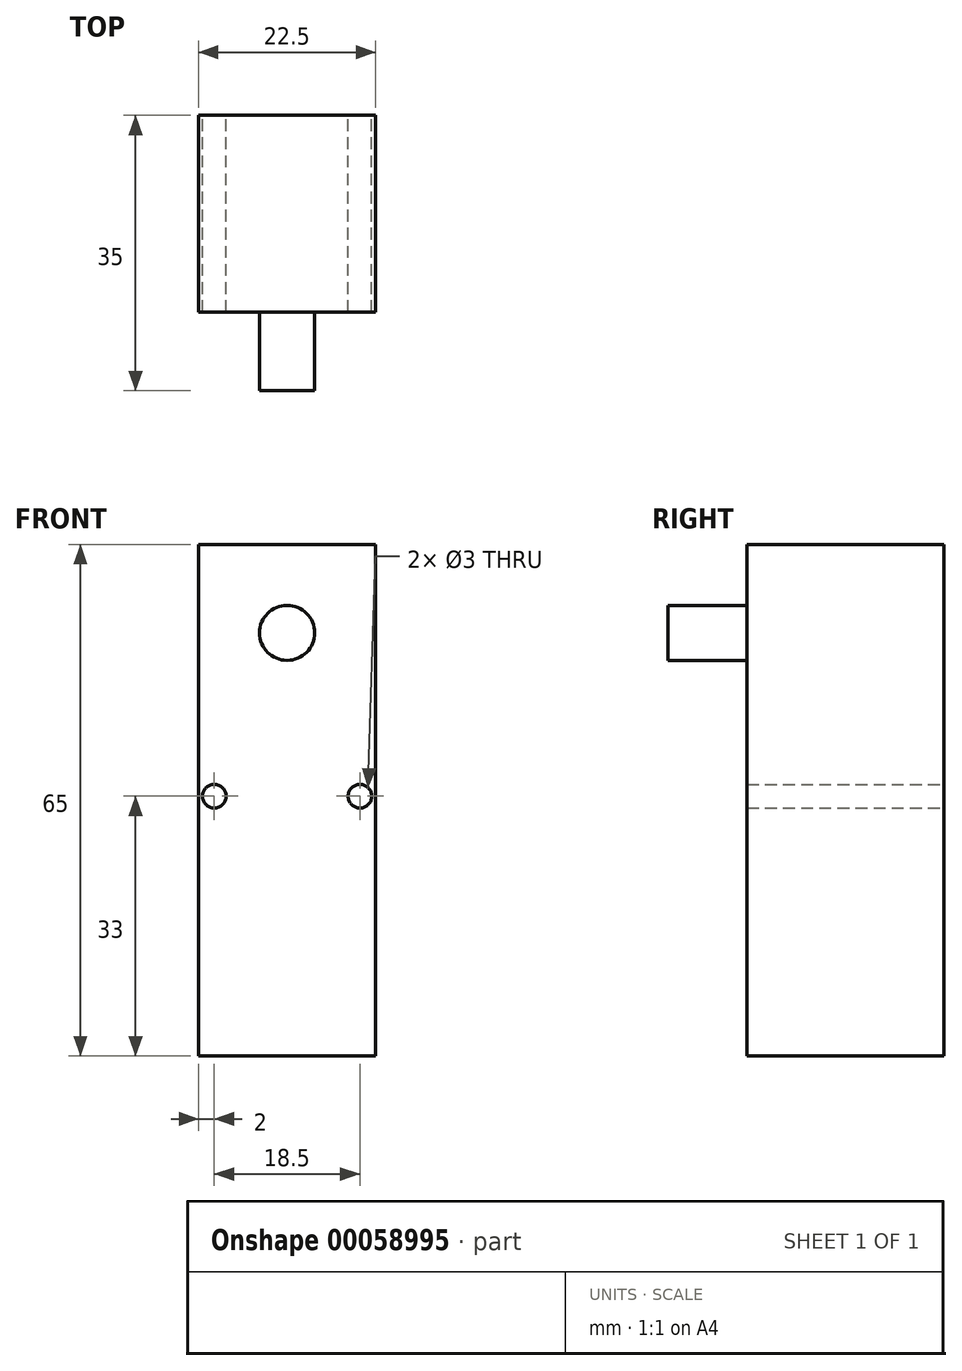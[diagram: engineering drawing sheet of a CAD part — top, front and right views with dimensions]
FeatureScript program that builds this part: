
annotation { "Feature Type Name" : "Feature", "Feature Type Description" : "" }
export const myFeature = defineFeature(function(context is Context, id is Id, definition is map)
    precondition{}
    {
        {
            var Q0;
            Q0=qCreatedBy(makeId("Front.planeOp"),FACE);
            var sketch = newSketch(context, id + "F0", { "sketchPlane" : qUnion([Q0])});
            skLineSegment(sketch, "E0.bottom", {"start": v(-11.25, 32.5) * mm, "end": v(11.25, 32.5) * mm});
            skLineSegment(sketch, "E0.top", {"start": v(-11.25, -32.5) * mm, "end": v(11.25, -32.5) * mm});
            skLineSegment(sketch, "E0.left", {"start": v(-11.25, 32.5) * mm, "end": v(-11.25, -32.5) * mm});
            skLineSegment(sketch, "E0.right", {"start": v(11.25, 32.5) * mm, "end": v(11.25, -32.5) * mm});
            skPoint(sketch, "E0.middle", {"position": v(0, 0) * mm});
            skCircle(sketch, "E1", {"center": v(9.25, 0.5) * mm, "radius": 1.5 * mm});
            skCircle(sketch, "E2.MirrorC", {"center": v(-9.25, 0.5) * mm, "radius": 1.5 * mm});
            skSolve(sketch);
        }
        {
            var Q0;
            Q0=qSketchRegion(id+"F0",true);
            extrude(context, id + "F1", {"entities" : qUnion([Q0]), "depth" : 25 * mm});
        }
        {
            var Q0;
            Q0=makeQuery(id+"F1.opExtrude","CAP_FACE",FACE,{"disambiguationData":[OSD([sQuery(id+"F0.wireOp",EDGE,"E0.bottom"),sQuery(id+"F0.wireOp",EDGE,"E0.top"),sQuery(id+"F0.wireOp",EDGE,"E0.left"),sQuery(id+"F0.wireOp",EDGE,"E0.right"),sQuery(id+"F0.wireOp",EDGE,"E1"),sQuery(id+"F0.wireOp",EDGE,"E2.MirrorC")])],"isStart":false});
            var sketch = newSketch(context, id + "F2", { "sketchPlane" : qUnion([Q0])});
            skCircle(sketch, "E3", {"center": v(0, 21.25) * mm, "radius": 3.5 * mm});
            skSolve(sketch);
        }
        {
            var Q0;
            Q0=qSketchRegion(id+"F2",true);
            extrude(context, id + "F3", {"entities" : qUnion([Q0]), "operationType" : NewBodyOperationType.ADD, "depth" : 10 * mm});
        }
    });
